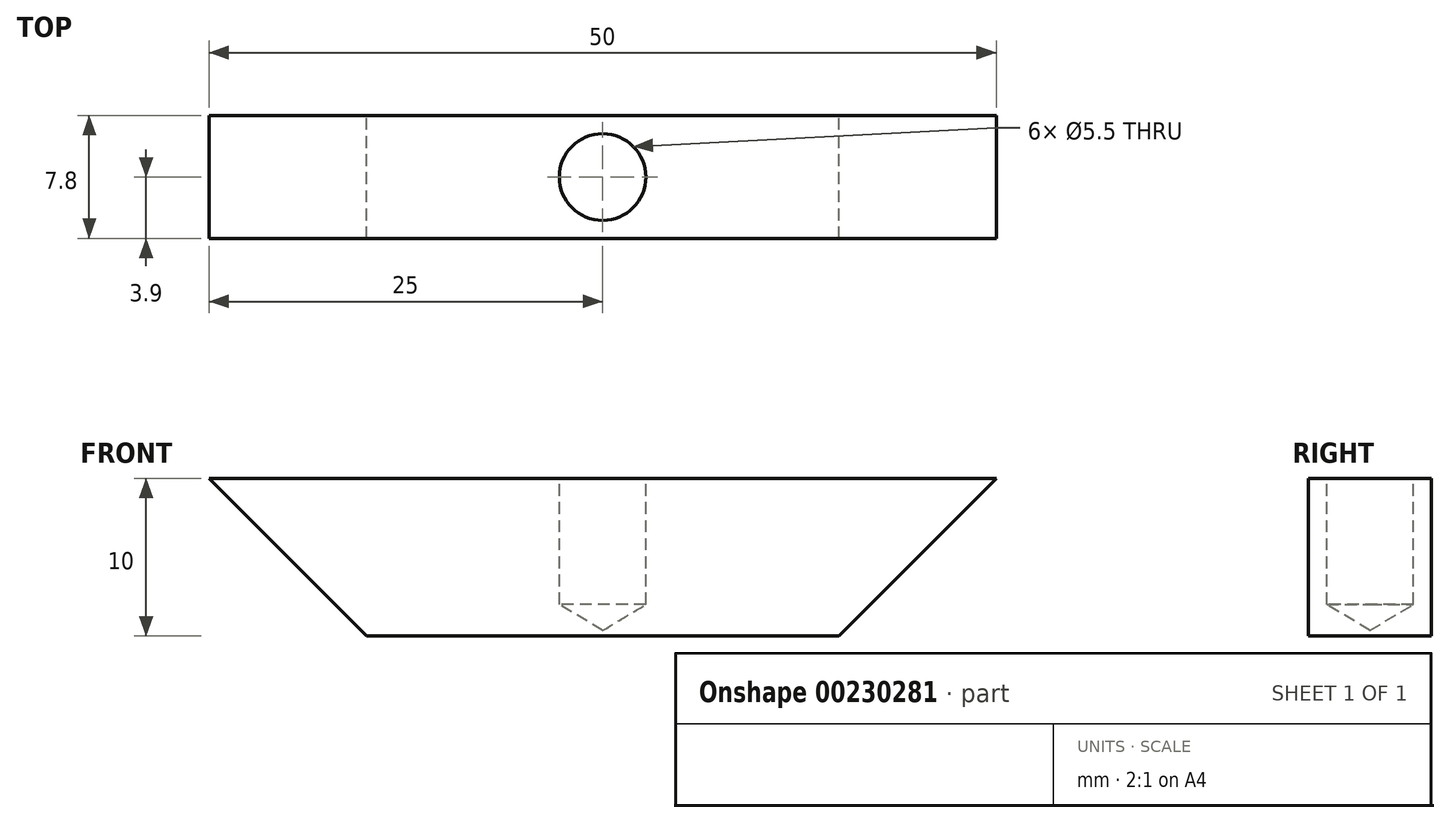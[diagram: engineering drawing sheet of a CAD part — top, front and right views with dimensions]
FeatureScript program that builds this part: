
annotation { "Feature Type Name" : "Feature", "Feature Type Description" : "" }
export const myFeature = defineFeature(function(context is Context, id is Id, definition is map)
    precondition{}
    {
        {
            var Q0;
            Q0=qCreatedBy(makeId("Front.planeOp"),FACE);
            var sketch = newSketch(context, id + "F0", { "sketchPlane" : qUnion([Q0])});
            skLineSegment(sketch, "E0", {"start": v(-15, 0) * mm, "end": v(15, 0) * mm});
            skLineSegment(sketch, "E1", {"start": v(15, 0) * mm, "end": v(25, 10) * mm});
            skLineSegment(sketch, "E2", {"start": v(25, 10) * mm, "end": v(-25, 10) * mm});
            skLineSegment(sketch, "E3", {"start": v(-25, 10) * mm, "end": v(-15, 0) * mm});
            skSolve(sketch);
        }
        {
            var Q0;
            Q0=makeQuery(id+"F0.imprint","IMPRINT",FACE,{"disambiguationData":[TD([[makeQuery(id+"F0.imprint","IMPRINT",EDGE,{"derivedFrom":sQuery(id+"F0.wireOp",EDGE,"E0")}),1.0]])]});
            extrude(context, id + "F1", {"entities" : qUnion([Q0]), "endBound" : BoundingType.SYMMETRIC, "depth" : 7.8 * mm});
        }
        {
            var Q0;
            Q0=makeQuery(id+"F1.opExtrude","SWEPT_FACE",FACE,{"disambiguationData":[OSD([sQuery(id+"F0.wireOp",EDGE,"E2")])]});
            var sketch = newSketch(context, id + "F2", { "sketchPlane" : qUnion([Q0])});
            skPoint(sketch, "E4", {"position": v(0, 0) * mm});
            skSolve(sketch);
        }
        {
            var Q0;
            Q0=sQuery(id+"F2.wireOp",VERTEX,"E4");
            var Q1;
            Q1=makeQuery(id+"F1.opExtrude","SWEPT_BODY",BODY,{"disambiguationData":[OSD([sQuery(id+"F0.wireOp",EDGE,"E0"),sQuery(id+"F0.wireOp",EDGE,"E1"),sQuery(id+"F0.wireOp",EDGE,"E2"),sQuery(id+"F0.wireOp",EDGE,"E3")])]});
            hole(context, id + "F3", {"style" : HoleStyle.SIMPLE, "endStyle" : HoleEndStyle.BLIND, "standardTappedOrClearance" : lookupTablePath({ "standard" : "ISO", "fit" : "Normal", "size" : "M5", "type" : "Clearance" }), "standardBlindInLast" : lookupTablePath({ "fit" : "Standard", "standard" : "ISO", "size" : "M5", "type" : "Clearance" }), "holeDiameter" : 5.5 * mm, "holeDepth" : 8 * mm, "locations" : qUnion([Q0]), "scope" : qUnion([Q1])});
        }
    });
